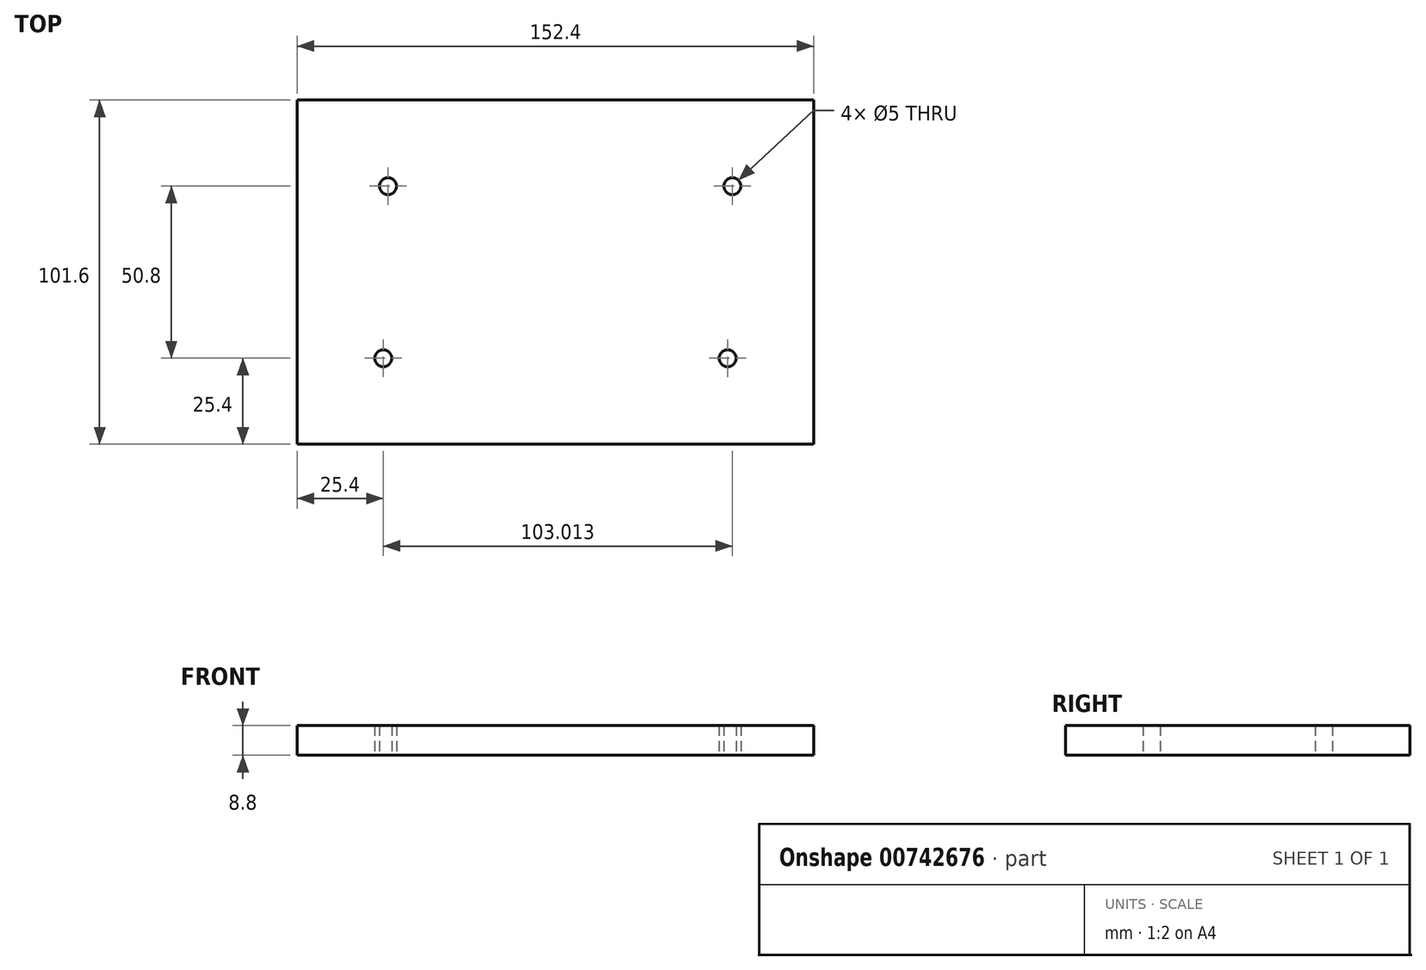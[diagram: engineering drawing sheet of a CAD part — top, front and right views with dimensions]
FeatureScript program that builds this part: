
annotation { "Feature Type Name" : "Feature", "Feature Type Description" : "" }
export const myFeature = defineFeature(function(context is Context, id is Id, definition is map)
    precondition{}
    {
        {
            var Q0;
            Q0=qCreatedBy(makeId("Top.planeOp"),FACE);
            var sketch = newSketch(context, id + "F0", { "sketchPlane" : qUnion([Q0])});
            skLineSegment(sketch, "E0.bottom", {"start": v(0, 0) * mm, "end": v(152.4, 0) * mm});
            skLineSegment(sketch, "E0.top", {"start": v(0, 101.6) * mm, "end": v(152.4, 101.6) * mm});
            skLineSegment(sketch, "E0.left", {"start": v(0, 0) * mm, "end": v(0, 101.6) * mm});
            skLineSegment(sketch, "E0.right", {"start": v(152.4, 0) * mm, "end": v(152.4, 101.6) * mm});
            skCircle(sketch, "E1", {"center": v(127, 25.4) * mm, "radius": 2.5 * mm});
            skCircle(sketch, "E2", {"center": v(25.4, 25.4) * mm, "radius": 2.5 * mm});
            skCircle(sketch, "E3", {"center": v(26.81, 76.2) * mm, "radius": 2.5 * mm});
            skCircle(sketch, "E4", {"center": v(128.41, 76.2) * mm, "radius": 2.5 * mm});
            skSolve(sketch);
        }
        {
            var Q0;
            Q0=makeQuery(id+"F0.imprint","IMPRINT",FACE,{"disambiguationData":[TD([[makeQuery(id+"F0.imprint","IMPRINT",EDGE,{"derivedFrom":sQuery(id+"F0.wireOp",EDGE,"E0.bottom")}),1.0]])]});
            extrude(context, id + "F1", {"entities" : qUnion([Q0]), "depth" : 8.8 * mm, "offsetDistance" : 25.4 * mm});
        }
    });
